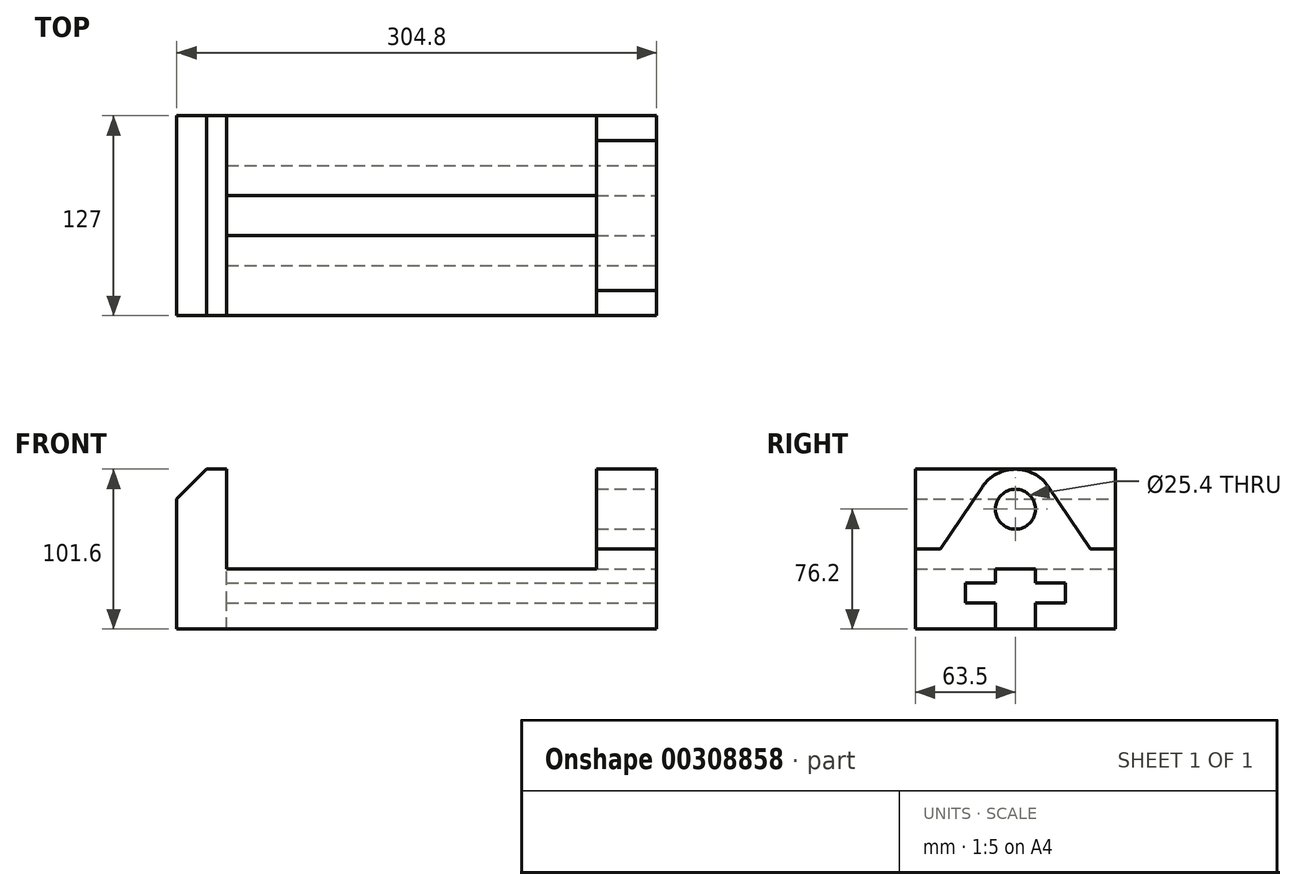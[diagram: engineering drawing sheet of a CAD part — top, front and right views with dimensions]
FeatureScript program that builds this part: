
annotation { "Feature Type Name" : "Feature", "Feature Type Description" : "" }
export const myFeature = defineFeature(function(context is Context, id is Id, definition is map)
    precondition{}
    {
        {
            var Q0;
            Q0=qCreatedBy(makeId("Front.planeOp"),FACE);
            var sketch = newSketch(context, id + "F0", { "sketchPlane" : qUnion([Q0])});
            skLineSegment(sketch, "E0", {"start": v(0, 0) * mm, "end": v(0, 101.6) * mm});
            skLineSegment(sketch, "E1", {"start": v(0, 101.6) * mm, "end": v(31.75, 101.6) * mm});
            skLineSegment(sketch, "E2", {"start": v(31.75, 101.6) * mm, "end": v(31.75, 38.1) * mm});
            skLineSegment(sketch, "E3", {"start": v(31.75, 38.1) * mm, "end": v(266.7, 38.1) * mm});
            skLineSegment(sketch, "E4", {"start": v(266.7, 38.1) * mm, "end": v(266.7, 101.6) * mm});
            skLineSegment(sketch, "E5", {"start": v(266.7, 101.6) * mm, "end": v(304.8, 101.6) * mm});
            skLineSegment(sketch, "E6", {"start": v(304.8, 101.6) * mm, "end": v(304.8, 0) * mm});
            skLineSegment(sketch, "E7", {"start": v(304.8, 0) * mm, "end": v(0, 0) * mm});
            skSolve(sketch);
        }
        {
            var Q0;
            Q0 = qSketchRegion(id + "F0", true);
            extrude(context, id + "F1", {"entities" : qUnion([Q0]), "depth" : 127 * mm});
        }
        {
            var Q0;
            Q0=makeQuery(id+"F1.opExtrude","SWEPT_EDGE",EDGE,{"disambiguationData":[OSD([sQuery(id+"F0.wireOp",EDGE,"E0"),sQuery(id+"F0.wireOp",EDGE,"E1")])]});
            chamfer(context, id + "F2", {"entities" : qUnion([Q0]), "chamferType" : ChamferType.TWO_OFFSETS, "width1" : 19.05 * mm, "oppositeDirection" : false, "width2" : 19.05 * mm, "tangentPropagation" : true});
        }
        {
            var Q0;
            Q0=makeQuery(id+"F1.opExtrude","SWEPT_FACE",FACE,{"disambiguationData":[OSD([sQuery(id+"F0.wireOp",EDGE,"E6")])]});
            var sketch = newSketch(context, id + "F3", { "sketchPlane" : qUnion([Q0])});
            skLineSegment(sketch, "E8", {"start": v(0, 50.8) * mm, "end": v(-15.87, 50.8) * mm});
            skLineSegment(sketch, "E9", {"start": v(-15.87, 50.8) * mm, "end": v(-42.4, 90.35) * mm});
            skLineSegment(sketch, "E10", {"start": v(-127, 50.8) * mm, "end": v(-111.12, 50.8) * mm});
            skLineSegment(sketch, "E11", {"start": v(-111.12, 50.8) * mm, "end": v(-84.6, 90.35) * mm});
            skArc(sketch, "E12", {"start": v(-42.4, 90.35) * mm, "mid": v(-63.5, 101.6) * mm, "end": v(-84.6, 90.35) * mm});
            skCircle(sketch, "E13", {"center": v(-63.5, 76.2) * mm, "radius": 12.7 * mm});
            skLineSegment(sketch, "E14", {"start": v(-63.5, 76.2) * mm, "end": v(-63.5, -10.2) * mm, "construction": true});
            skPoint(sketch, "E14.endSnap0", {"position": v(-63.5, 0) * mm});
            skLineSegment(sketch, "E15", {"start": v(-76.2, 0) * mm, "end": v(-76.2, 16.5) * mm});
            skLineSegment(sketch, "E16", {"start": v(-76.2, 16.5) * mm, "end": v(-95.25, 16.5) * mm});
            skLineSegment(sketch, "E17", {"start": v(-95.25, 16.5) * mm, "end": v(-95.25, 29.2) * mm});
            skLineSegment(sketch, "E18", {"start": v(-95.25, 29.2) * mm, "end": v(-76.2, 29.2) * mm});
            skLineSegment(sketch, "E19", {"start": v(-76.2, 29.2) * mm, "end": v(-76.2, 38.1) * mm});
            skLineSegment(sketch, "E20", {"start": v(-76.2, 38.1) * mm, "end": v(-63.5, 38.1) * mm});
            skLineSegment(sketch, "E21.MirrorCS", {"start": v(-50.8, 38.1) * mm, "end": v(-63.5, 38.1) * mm});
            skLineSegment(sketch, "E22.MirrorCS", {"start": v(-50.8, 29.2) * mm, "end": v(-50.8, 38.1) * mm});
            skLineSegment(sketch, "E23.MirrorCS", {"start": v(-31.75, 29.21) * mm, "end": v(-50.8, 29.2) * mm});
            skLineSegment(sketch, "E24.MirrorCS", {"start": v(-31.75, 16.5) * mm, "end": v(-31.75, 29.2) * mm});
            skLineSegment(sketch, "E25.MirrorCS", {"start": v(-50.8, 16.5) * mm, "end": v(-31.75, 16.5) * mm});
            skLineSegment(sketch, "E26.MirrorCS", {"start": v(-50.8, 0) * mm, "end": v(-50.8, 16.5) * mm});
            skLineSegment(sketch, "E27", {"start": v(-76.2, 0) * mm, "end": v(-63.5, 0) * mm});
            skLineSegment(sketch, "E28.MirrorCS", {"start": v(-50.8, 0) * mm, "end": v(-63.5, 0) * mm});
            skSolve(sketch);
        }
        {
            var Q0;
            Q0 = qSketchRegion(id + "F3", true);
            var Q1;
            {var subQ7=sQuery(id+"F3.wireOp",EDGE,"E10");Q1=makeQuery(id+"F3.imprint","IMPRINT",FACE,{"disambiguationData":[TD([[makeQuery(id+"F3.imprint","IMPRINT",EDGE,{"derivedFrom":subQ7}),1.0]])]});}
            var Q2;
            {var subQ7=sQuery(id+"F3.wireOp",EDGE,"E8");Q2=makeQuery(id+"F3.imprint","IMPRINT",FACE,{"disambiguationData":[TD([[makeQuery(id+"F3.imprint","IMPRINT",EDGE,{"derivedFrom":subQ7}),-1.0]])]});}
            extrude(context, id + "F4", {"entities" : qUnion([Q0, Q1, Q2]), "operationType" : NewBodyOperationType.REMOVE, "oppositeDirection" : true, "depth" : 273.05 * mm});
        }
    });
